# Revit family: 0047071
name_source: partatom
category: Lighting Fixtures
revit_build: Autodesk Revit 2017 (Build: 20160225_1515(x64)
units: mm (PartAtom-declared; Revit-internal decimal feet)

## family parameters
Cut with Voids When Loaded = No
Host = Face
Light Source = Yes
OmniClass Number = 23.80.70.00
OmniClass Title = Lighting
Part Type = Normal
Room Calculation Point = No
Round Connector Dimension = Use Diameter
Shared = No

## types (1)
- 0047071 START ECO PANEL 1200X300 3200LM 830
    Apparent Load = 36 VA
    Area+xL_SYL = 1156 mm
    Area+xW_SYL = 256 mm  [stored 0.839895 ft]
    Area-xL_SYL = 1146 mm  [stored 3.75984 ft]
    Area-xW_SYL = 246 mm
    Assembly Code = D5020200
    AssetType = Fixed
    ClassificationName = Uniclass2015
    ClassificationValue = EF_70_80
    Color Filter = 16777215
    Cost = 0 $
    Default Elevation = 1219 mm
    Dimming Lamp Color Temperature Shift = <None>
    DocumentationLiterature = http://www.sylvania-lighting.com
    ElectricShockClassification = Class II
    Emit Shape Visible in Rendering = No
    Emit from Rectangle Length = 553 mm  [stored 1.8143 ft]
    Emit from Rectangle Width = 553 mm  [stored 1.8143 ft]
    IfcExportAs = IfcLightFixtureType
    IfcExportType = IfcLightFixtureType
    ImpactProtectionIndex = IK02
    IngressProtection = IP40/20
    Keynote = 16500
    Lamp = LED
    LampColourRenderingIndex = 80
    LampColourTemperature = 3000 K
    LampMacAdamStep = 6
    LampNominalLuminous = 3200 lm
    LampsType = LED
    Length01_SYL = 1195 mm  [stored 3.9206 ft]
    LumAreaL_SYL = 1151 mm  [stored 3.77625 ft]
    LumAreaW_SYL = 251 mm  [stored 0.823491 ft]
    LumArea_SYL = 551 mm
    LuminousEfficacy = 89 lm/W
    Manufacturer = Feilo Sylvania
    ManufacturerName = Feilo Sylvania
    Material = aluminium,steel housing, other diffuser
    Material_1_SYL = PC/ABS Plastic
    Material_2_SYL = LED
    Material_3_SYL = <By Category>
    Material_4_SYL = <By Category>
    Model = START eco Panel 1200x300 3200Lm 830
    ModelNumber = 0047071
    ModelReference = START eco Panel 1200x300 3200Lm 830
    Name = START eco Panel 1200x300 3200Lm 830
    NominalDepth = 300 mm
    NominalHeight = 34 mm
    NominalLength = 1200 mm
    Photometric Web File = 0047071.ies
    PowerConsumption = 36 W
    PowerFactor = 0.95
    Tilt Angle = -90.00°
    Type Image = <None>
    TypeName = START eco Panel 1200x300 3200Lm 830
    URL = http://www.sylvania-lighting.com
    Voltage = 0 V
    Weight = 2.45 kg
    Width01_SYL = 295 mm

note: [stored X ft] marks values corroborated as IEEE doubles in the binary element streams (Revit-internal decimal feet)

## geometry (parser evidence)
native form markers: Sweep x3
no freeform markers — native parametric forms only
